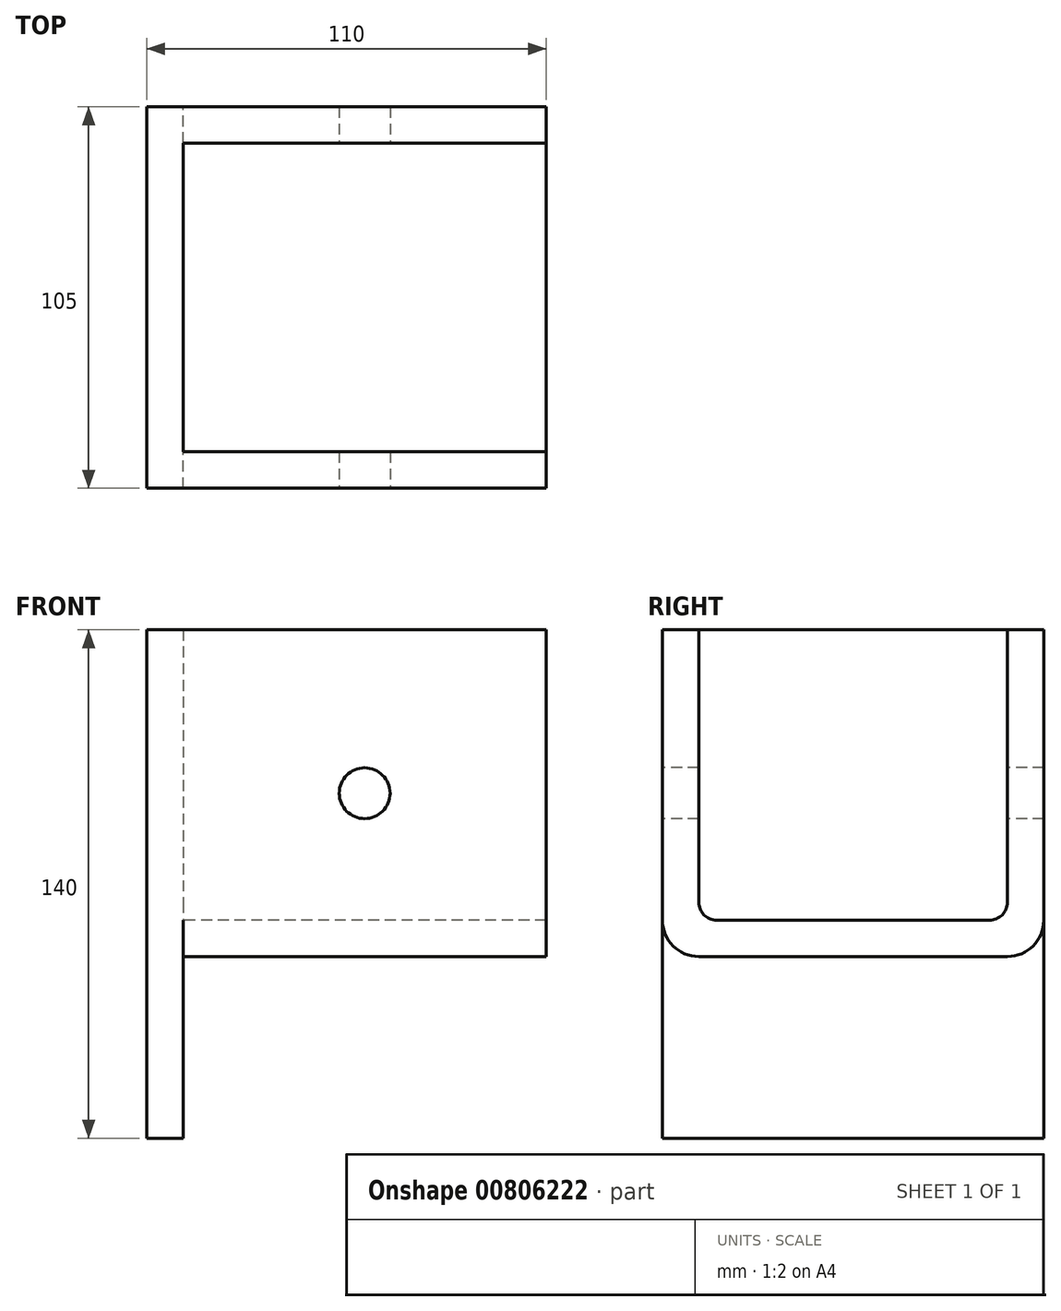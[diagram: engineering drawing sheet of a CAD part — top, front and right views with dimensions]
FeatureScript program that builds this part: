
annotation { "Feature Type Name" : "Feature", "Feature Type Description" : "" }
export const myFeature = defineFeature(function(context is Context, id is Id, definition is map)
    precondition{}
    {
        {
            var Q0;
            Q0=qCreatedBy(makeId("Right.planeOp"),FACE);
            var sketch = newSketch(context, id + "F0", { "sketchPlane" : qUnion([Q0])});
            skLineSegment(sketch, "E0.bottom", {"start": v(52.5, -45) * mm, "end": v(-52.5, -45) * mm});
            skLineSegment(sketch, "E0.top", {"start": v(52.5, 45) * mm, "end": v(-52.5, 45) * mm});
            skLineSegment(sketch, "E0.left", {"start": v(52.5, -45) * mm, "end": v(52.5, 45) * mm});
            skLineSegment(sketch, "E0.right", {"start": v(-52.5, -45) * mm, "end": v(-52.5, 45) * mm});
            skPoint(sketch, "E0.middle", {"position": v(0, 0) * mm});
            skSolve(sketch);
        }
        {
            var Q0;
            Q0=qSketchRegion(id+"F0",true);
            extrude(context, id + "F1", {"entities" : qUnion([Q0]), "depth" : 10 * mm, "offsetDistance" : 25 * mm});
        }
        {
            var Q0;
            Q0=makeQuery(id+"F1.opExtrude","CAP_FACE",FACE,{"disambiguationData":[OSD([sQuery(id+"F0.wireOp",EDGE,"E0.bottom"),sQuery(id+"F0.wireOp",EDGE,"E0.top"),sQuery(id+"F0.wireOp",EDGE,"E0.left"),sQuery(id+"F0.wireOp",EDGE,"E0.right")])],"isStart":false});
            var sketch = newSketch(context, id + "F2", { "sketchPlane" : qUnion([Q0])});
            skLineSegment(sketch, "E1.bottom", {"start": v(-52.5, 45) * mm, "end": v(52.5, 45) * mm});
            skLineSegment(sketch, "E1.top", {"start": v(-42.5, -45) * mm, "end": v(42.5, -45) * mm});
            skLineSegment(sketch, "E1.left", {"start": v(-52.5, 45) * mm, "end": v(-52.5, -35) * mm});
            skLineSegment(sketch, "E1.right", {"start": v(52.5, 45) * mm, "end": v(52.5, -35) * mm});
            skPoint(sketch, "E1.middle", {"position": v(0, 0) * mm});
            skLineSegment(sketch, "E2.0", {"start": v(42.5, 45) * mm, "end": v(42.5, -30) * mm});
            skLineSegment(sketch, "E2.1", {"start": v(-37.5, -35) * mm, "end": v(37.5, -35) * mm});
            skLineSegment(sketch, "E2.2", {"start": v(-42.5, 45) * mm, "end": v(-42.5, -30) * mm});
            skPoint(sketch, "E3.visualSharp", {"position": v(-42.5, -35) * mm});
            skArc(sketch, "E3.filletArc", {"start": v(-42.5, -30) * mm, "mid": v(-41.04, -33.54) * mm, "end": v(-37.5, -35) * mm});
            skPoint(sketch, "E4.visualSharp", {"position": v(42.5, -35) * mm});
            skArc(sketch, "E4.filletArc", {"start": v(37.5, -35) * mm, "mid": v(41.04, -33.54) * mm, "end": v(42.5, -30) * mm});
            skPoint(sketch, "E5.visualSharp", {"position": v(52.5, -45) * mm});
            skArc(sketch, "E5.filletArc", {"start": v(42.5, -45) * mm, "mid": v(49.57, -42.07) * mm, "end": v(52.5, -35) * mm});
            skPoint(sketch, "E6.visualSharp", {"position": v(-52.5, -45) * mm});
            skArc(sketch, "E6.filletArc", {"start": v(-52.5, -35) * mm, "mid": v(-49.57, -42.07) * mm, "end": v(-42.5, -45) * mm});
            skSolve(sketch);
        }
        {
            var Q0;
            Q0=makeQuery(id+"F2.imprint","IMPRINT",FACE,{"disambiguationData":[TD([[makeQuery(id+"F2.imprint","IMPRINT",EDGE,{"derivedFrom":sQuery(id+"F2.wireOp",EDGE,"E1.top")}),-1.0]])]});
            extrude(context, id + "F3", {"entities" : qUnion([Q0]), "depth" : 100 * mm, "offsetDistance" : 25 * mm});
        }
        {
            var Q0;
            Q0=makeQuery(id+"F1.opExtrude","SWEPT_FACE",FACE,{"disambiguationData":[OSD([sQuery(id+"F0.wireOp",EDGE,"E0.bottom")])]});
            var sketch = newSketch(context, id + "F4", { "sketchPlane" : qUnion([Q0])});
            skLineSegment(sketch, "E7.bottom", {"start": v(10, -52.5) * mm, "end": v(0, -52.5) * mm});
            skLineSegment(sketch, "E7.top", {"start": v(10, 52.5) * mm, "end": v(0, 52.5) * mm});
            skLineSegment(sketch, "E7.left", {"start": v(10, -52.5) * mm, "end": v(10, 52.5) * mm});
            skLineSegment(sketch, "E7.right", {"start": v(0, -52.5) * mm, "end": v(0, 52.5) * mm});
            skSolve(sketch);
        }
        {
            var Q0;
            Q0=qSketchRegion(id+"F4",true);
            extrude(context, id + "F5", {"entities" : qUnion([Q0]), "operationType" : NewBodyOperationType.ADD, "depth" : 50 * mm, "offsetDistance" : 25 * mm});
        }
        {
            var Q0;
            Q0=qCreatedBy(makeId("Front.planeOp"),FACE);
            var sketch = newSketch(context, id + "F6", { "sketchPlane" : qUnion([Q0])});
            skLineSegment(sketch, "E8", {"start": v(0, 0) * mm, "end": v(60, 0) * mm});
            skCircle(sketch, "E9", {"center": v(60, 0) * mm, "radius": 7 * mm});
            skSolve(sketch);
        }
        {
            var Q0;
            Q0=qSketchRegion(id+"F6",true);
            var Q1;
            Q1=sQuery(id+"F6.wireOp",EDGE,"E9");
            extrude(context, id + "F7", {"entities" : qUnion([Q0]), "operationType" : NewBodyOperationType.REMOVE, "surfaceEntities" : qUnion([Q1]), "endBound" : BoundingType.SYMMETRIC, "oppositeDirection" : true, "depth" : 200 * mm, "offsetDistance" : 25 * mm});
        }
    });
